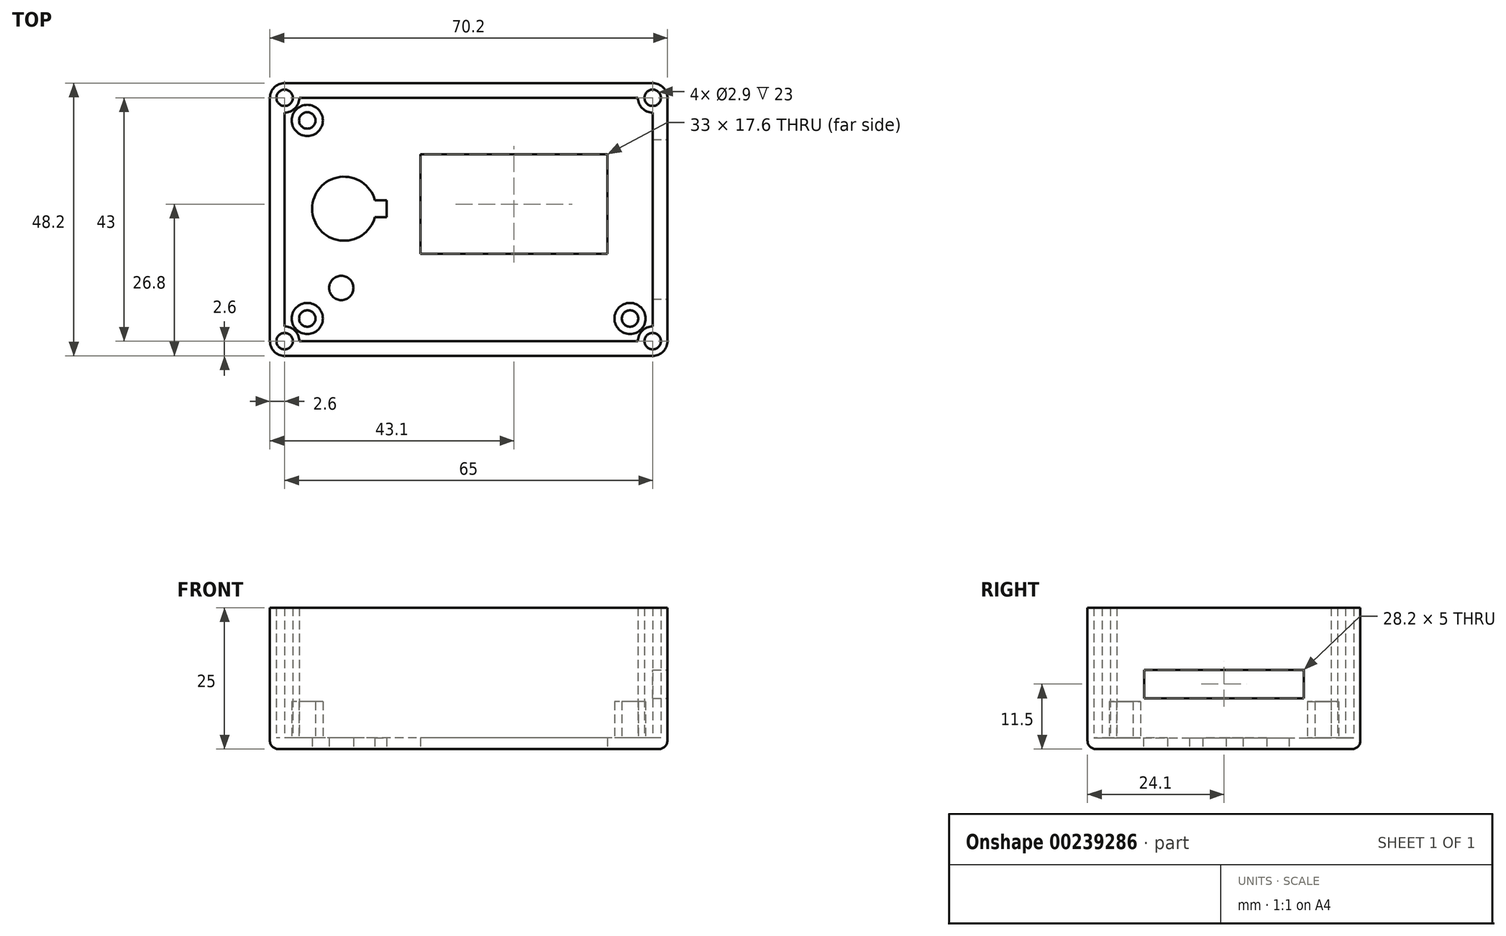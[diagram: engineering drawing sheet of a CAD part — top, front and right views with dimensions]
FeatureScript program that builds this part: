
annotation { "Feature Type Name" : "Feature", "Feature Type Description" : "" }
export const myFeature = defineFeature(function(context is Context, id is Id, definition is map)
    precondition{}
    {
        {
            var Q0;
            Q0=qCreatedBy(makeId("Top.planeOp"),FACE);
            var sketch = newSketch(context, id + "F0", { "sketchPlane" : qUnion([Q0])});
            skLineSegment(sketch, "E0.bottom", {"start": v(35.1, -24.1) * mm, "end": v(-35.1, -24.1) * mm});
            skLineSegment(sketch, "E0.top", {"start": v(35.1, 24.1) * mm, "end": v(-35.1, 24.1) * mm});
            skLineSegment(sketch, "E0.left", {"start": v(35.1, -24.1) * mm, "end": v(35.1, 24.1) * mm});
            skLineSegment(sketch, "E0.right", {"start": v(-35.1, -24.1) * mm, "end": v(-35.1, 24.1) * mm});
            skPoint(sketch, "E0.middle", {"position": v(0, 0) * mm});
            skLineSegment(sketch, "E1.bottom", {"start": v(28.5, -17.5) * mm, "end": v(-28.5, -17.5) * mm});
            skLineSegment(sketch, "E1.top", {"start": v(28.5, 17.5) * mm, "end": v(-28.5, 17.5) * mm});
            skLineSegment(sketch, "E1.left", {"start": v(28.5, -17.5) * mm, "end": v(28.5, 17.5) * mm});
            skLineSegment(sketch, "E1.right", {"start": v(-28.5, -17.5) * mm, "end": v(-28.5, 17.5) * mm});
            skLineSegment(sketch, "E2.bottom", {"start": v(-32.5, 21.5) * mm, "end": v(32.5, 21.5) * mm});
            skLineSegment(sketch, "E2.top", {"start": v(-32.5, -21.5) * mm, "end": v(32.5, -21.5) * mm});
            skLineSegment(sketch, "E2.left", {"start": v(-32.5, 21.5) * mm, "end": v(-32.5, -21.5) * mm});
            skLineSegment(sketch, "E2.right", {"start": v(32.5, 21.5) * mm, "end": v(32.5, -21.5) * mm});
            skCircle(sketch, "E3", {"center": v(-32.5, 21.5) * mm, "radius": 2.6 * mm});
            skCircle(sketch, "E4", {"center": v(-32.5, -21.5) * mm, "radius": 2.6 * mm});
            skCircle(sketch, "E5", {"center": v(32.5, -21.5) * mm, "radius": 2.6 * mm});
            skCircle(sketch, "E6", {"center": v(32.5, -21.5) * mm, "radius": 1.45 * mm});
            skCircle(sketch, "E7", {"center": v(-32.5, -21.5) * mm, "radius": 1.45 * mm});
            skCircle(sketch, "E8", {"center": v(32.5, 21.5) * mm, "radius": 2.6 * mm});
            skCircle(sketch, "E9", {"center": v(32.5, 21.5) * mm, "radius": 1.45 * mm});
            skCircle(sketch, "E10", {"center": v(-32.5, 21.5) * mm, "radius": 1.45 * mm});
            skCircle(sketch, "E11", {"center": v(-28.5, 17.5) * mm, "radius": 2.75 * mm});
            skCircle(sketch, "E12", {"center": v(-28.5, 17.5) * mm, "radius": 1.45 * mm});
            skCircle(sketch, "E13", {"center": v(28.5, -17.5) * mm, "radius": 1.45 * mm});
            skCircle(sketch, "E14", {"center": v(28.5, -17.5) * mm, "radius": 2.75 * mm});
            skCircle(sketch, "E15", {"center": v(-28.5, -17.5) * mm, "radius": 1.45 * mm});
            skCircle(sketch, "E16", {"center": v(-28.5, -17.5) * mm, "radius": 2.75 * mm});
            skCircle(sketch, "E17", {"center": v(-22, 1.9) * mm, "radius": 5.65 * mm});
            skCircle(sketch, "E18", {"center": v(-22.5, -12.1) * mm, "radius": 2.15 * mm});
            skLineSegment(sketch, "E19.bottom", {"start": v(24.5, -6.1) * mm, "end": v(-8.5, -6.1) * mm});
            skLineSegment(sketch, "E19.top", {"start": v(24.5, 11.5) * mm, "end": v(-8.5, 11.5) * mm});
            skLineSegment(sketch, "E19.left", {"start": v(24.5, -6.1) * mm, "end": v(24.5, 11.5) * mm});
            skLineSegment(sketch, "E19.right", {"start": v(-8.5, -6.1) * mm, "end": v(-8.5, 11.5) * mm});
            skPoint(sketch, "E19.middle", {"position": v(8, 2.7) * mm});
            skLineSegment(sketch, "E20.bottom", {"start": v(-22, 3.4) * mm, "end": v(-14.5, 3.4) * mm});
            skLineSegment(sketch, "E20.top", {"start": v(-22, 0.4) * mm, "end": v(-14.5, 0.4) * mm});
            skLineSegment(sketch, "E20.left", {"start": v(-22, 3.4) * mm, "end": v(-22, 0.4) * mm});
            skLineSegment(sketch, "E20.right", {"start": v(-14.5, 3.4) * mm, "end": v(-14.5, 0.4) * mm});
            skSolve(sketch);
        }
        {
            var Q0;
            {var subQ0=sQuery(id+"F0.wireOp",EDGE,"E1.right");var subQ1=sQuery(id+"F0.wireOp",EDGE,"E1.bottom");var subQ2=makeQuery(id+"F0.imprint","INTERSECT",VERTEX,{"derivedFrom":[subQ1,subQ0]});Q0=makeQuery(id+"F0.imprint","IMPRINT",FACE,{"disambiguationData":[TD([[makeQuery(id+"F0.imprint","IMPRINT",EDGE,{"disambiguationData":[TD([[subQ2,1.0]])],"derivedFrom":subQ1}),1.0]])]});}
            var Q1;
            {var subQ0=sQuery(id+"F0.wireOp",EDGE,"E1.right");var subQ1=sQuery(id+"F0.wireOp",EDGE,"E1.bottom");var subQ2=makeQuery(id+"F0.imprint","INTERSECT",VERTEX,{"derivedFrom":[subQ1,subQ0]});Q1=makeQuery(id+"F0.imprint","IMPRINT",FACE,{"disambiguationData":[TD([[makeQuery(id+"F0.imprint","IMPRINT",EDGE,{"disambiguationData":[TD([[subQ2,1.0]])],"derivedFrom":subQ1}),-1.0]])]});}
            var Q2;
            {var subQ5=sQuery(id+"F0.wireOp",EDGE,"E2.top");var subQ8=sQuery(id+"F0.wireOp",EDGE,"E7");var subQ10=makeQuery(id+"F0.imprint","INTERSECT",VERTEX,{"derivedFrom":[subQ5,subQ8]});Q2=makeQuery(id+"F0.imprint","IMPRINT",FACE,{"disambiguationData":[TD([[makeQuery(id+"F0.imprint","IMPRINT",EDGE,{"disambiguationData":[TD([[subQ10,-1.0]])],"derivedFrom":subQ5}),1.0]])]});}
            var Q3;
            {var subQ0=sQuery(id+"F0.wireOp",EDGE,"E2.left");var subQ1=sQuery(id+"F0.wireOp",EDGE,"E2.top");var subQ2=makeQuery(id+"F0.imprint","INTERSECT",VERTEX,{"derivedFrom":[subQ1,subQ0]});Q3=makeQuery(id+"F0.imprint","IMPRINT",FACE,{"disambiguationData":[TD([[makeQuery(id+"F0.imprint","IMPRINT",EDGE,{"disambiguationData":[TD([[subQ2,-1.0]])],"derivedFrom":subQ1}),1.0]])]});}
            var Q4;
            {var subQ0=sQuery(id+"F0.wireOp",EDGE,"E2.left");var subQ1=sQuery(id+"F0.wireOp",EDGE,"E2.top");var subQ2=makeQuery(id+"F0.imprint","INTERSECT",VERTEX,{"derivedFrom":[subQ1,subQ0]});Q4=makeQuery(id+"F0.imprint","IMPRINT",FACE,{"disambiguationData":[TD([[makeQuery(id+"F0.imprint","IMPRINT",EDGE,{"disambiguationData":[TD([[subQ2,-1.0]])],"derivedFrom":subQ1}),-1.0]])]});}
            var Q5;
            {var subQ3=sQuery(id+"F0.wireOp",EDGE,"E7");var subQ4=sQuery(id+"F0.wireOp",EDGE,"E2.top");var subQ5=makeQuery(id+"F0.imprint","INTERSECT",VERTEX,{"derivedFrom":[subQ4,subQ3]});Q5=makeQuery(id+"F0.imprint","IMPRINT",FACE,{"disambiguationData":[TD([[makeQuery(id+"F0.imprint","IMPRINT",EDGE,{"disambiguationData":[TD([[subQ5,-1.0]])],"derivedFrom":subQ4}),-1.0]])]});}
            var Q6;
            {var subQ0=sQuery(id+"F0.wireOp",EDGE,"E5");var subQ1=sQuery(id+"F0.wireOp",EDGE,"E0.bottom");var subQ2=makeQuery(id+"F0.imprint","INTERSECT",VERTEX,{"derivedFrom":[subQ1,subQ0]});Q6=makeQuery(id+"F0.imprint","IMPRINT",FACE,{"disambiguationData":[TD([[makeQuery(id+"F0.imprint","IMPRINT",EDGE,{"disambiguationData":[TD([[subQ2,-1.0]])],"derivedFrom":subQ1}),-1.0]])]});}
            var Q7;
            {var subQ0=sQuery(id+"F0.wireOp",EDGE,"E4");var subQ1=sQuery(id+"F0.wireOp",EDGE,"E0.right");var subQ2=makeQuery(id+"F0.imprint","INTERSECT",VERTEX,{"derivedFrom":[subQ1,subQ0]});Q7=makeQuery(id+"F0.imprint","IMPRINT",FACE,{"disambiguationData":[TD([[makeQuery(id+"F0.imprint","IMPRINT",EDGE,{"disambiguationData":[TD([[subQ2,-1.0]])],"derivedFrom":subQ1}),-1.0]])]});}
            var Q8;
            {var subQ0=sQuery(id+"F0.wireOp",EDGE,"E8");var subQ5=sQuery(id+"F0.wireOp",EDGE,"E2.bottom");var subQ6=makeQuery(id+"F0.imprint","INTERSECT",VERTEX,{"derivedFrom":[subQ5,subQ0]});Q8=makeQuery(id+"F0.imprint","IMPRINT",FACE,{"disambiguationData":[TD([[makeQuery(id+"F0.imprint","IMPRINT",EDGE,{"disambiguationData":[TD([[subQ6,-1.0]])],"derivedFrom":subQ5}),-1.0]])]});}
            var Q9;
            {var subQ0=sQuery(id+"F0.wireOp",EDGE,"E2.right");var subQ1=sQuery(id+"F0.wireOp",EDGE,"E2.bottom");var subQ2=makeQuery(id+"F0.imprint","INTERSECT",VERTEX,{"derivedFrom":[subQ1,subQ0]});Q9=makeQuery(id+"F0.imprint","IMPRINT",FACE,{"disambiguationData":[TD([[makeQuery(id+"F0.imprint","IMPRINT",EDGE,{"disambiguationData":[TD([[subQ2,1.0]])],"derivedFrom":subQ1}),-1.0]])]});}
            var Q10;
            {var subQ0=sQuery(id+"F0.wireOp",EDGE,"E2.right");var subQ1=sQuery(id+"F0.wireOp",EDGE,"E2.bottom");var subQ2=makeQuery(id+"F0.imprint","INTERSECT",VERTEX,{"derivedFrom":[subQ1,subQ0]});Q10=makeQuery(id+"F0.imprint","IMPRINT",FACE,{"disambiguationData":[TD([[makeQuery(id+"F0.imprint","IMPRINT",EDGE,{"disambiguationData":[TD([[subQ2,1.0]])],"derivedFrom":subQ1}),1.0]])]});}
            var Q11;
            {var subQ0=sQuery(id+"F0.wireOp",EDGE,"E8");var subQ2=sQuery(id+"F0.wireOp",EDGE,"E2.bottom");var subQ3=makeQuery(id+"F0.imprint","INTERSECT",VERTEX,{"derivedFrom":[subQ2,subQ0]});Q11=makeQuery(id+"F0.imprint","IMPRINT",FACE,{"disambiguationData":[TD([[makeQuery(id+"F0.imprint","IMPRINT",EDGE,{"disambiguationData":[TD([[subQ3,-1.0]])],"derivedFrom":subQ2}),1.0]])]});}
            var Q12;
            {var subQ0=sQuery(id+"F0.wireOp",EDGE,"E5");var subQ1=sQuery(id+"F0.wireOp",EDGE,"E0.left");var subQ2=makeQuery(id+"F0.imprint","INTERSECT",VERTEX,{"derivedFrom":[subQ1,subQ0]});Q12=makeQuery(id+"F0.imprint","IMPRINT",FACE,{"disambiguationData":[TD([[makeQuery(id+"F0.imprint","IMPRINT",EDGE,{"disambiguationData":[TD([[subQ2,-1.0]])],"derivedFrom":subQ1}),1.0]])]});}
            var Q13;
            {var subQ0=sQuery(id+"F0.wireOp",EDGE,"E8");var subQ1=sQuery(id+"F0.wireOp",EDGE,"E0.top");var subQ2=makeQuery(id+"F0.imprint","INTERSECT",VERTEX,{"derivedFrom":[subQ1,subQ0]});Q13=makeQuery(id+"F0.imprint","IMPRINT",FACE,{"disambiguationData":[TD([[makeQuery(id+"F0.imprint","IMPRINT",EDGE,{"disambiguationData":[TD([[subQ2,-1.0]])],"derivedFrom":subQ1}),1.0]])]});}
            var Q14;
            {var subQ2=sQuery(id+"F0.wireOp",EDGE,"E2.bottom");var subQ5=sQuery(id+"F0.wireOp",EDGE,"E10");var subQ9=makeQuery(id+"F0.imprint","INTERSECT",VERTEX,{"derivedFrom":[subQ2,subQ5]});Q14=makeQuery(id+"F0.imprint","IMPRINT",FACE,{"disambiguationData":[TD([[makeQuery(id+"F0.imprint","IMPRINT",EDGE,{"disambiguationData":[TD([[subQ9,-1.0]])],"derivedFrom":subQ2}),1.0]])]});}
            var Q15;
            {var subQ0=sQuery(id+"F0.wireOp",EDGE,"E2.left");var subQ1=sQuery(id+"F0.wireOp",EDGE,"E2.bottom");var subQ2=makeQuery(id+"F0.imprint","INTERSECT",VERTEX,{"derivedFrom":[subQ1,subQ0]});Q15=makeQuery(id+"F0.imprint","IMPRINT",FACE,{"disambiguationData":[TD([[makeQuery(id+"F0.imprint","IMPRINT",EDGE,{"disambiguationData":[TD([[subQ2,-1.0]])],"derivedFrom":subQ1}),1.0]])]});}
            var Q16;
            {var subQ0=sQuery(id+"F0.wireOp",EDGE,"E2.left");var subQ1=sQuery(id+"F0.wireOp",EDGE,"E2.bottom");var subQ2=makeQuery(id+"F0.imprint","INTERSECT",VERTEX,{"derivedFrom":[subQ1,subQ0]});Q16=makeQuery(id+"F0.imprint","IMPRINT",FACE,{"disambiguationData":[TD([[makeQuery(id+"F0.imprint","IMPRINT",EDGE,{"disambiguationData":[TD([[subQ2,-1.0]])],"derivedFrom":subQ1}),-1.0]])]});}
            var Q17;
            {var subQ1=sQuery(id+"F0.wireOp",EDGE,"E2.bottom");var subQ5=sQuery(id+"F0.wireOp",EDGE,"E10");var subQ10=makeQuery(id+"F0.imprint","INTERSECT",VERTEX,{"derivedFrom":[subQ1,subQ5]});Q17=makeQuery(id+"F0.imprint","IMPRINT",FACE,{"disambiguationData":[TD([[makeQuery(id+"F0.imprint","IMPRINT",EDGE,{"disambiguationData":[TD([[subQ10,-1.0]])],"derivedFrom":subQ1}),-1.0]])]});}
            var Q18;
            {var subQ0=sQuery(id+"F0.wireOp",EDGE,"E5");var subQ2=sQuery(id+"F0.wireOp",EDGE,"E2.top");var subQ3=makeQuery(id+"F0.imprint","INTERSECT",VERTEX,{"derivedFrom":[subQ2,subQ0]});Q18=makeQuery(id+"F0.imprint","IMPRINT",FACE,{"disambiguationData":[TD([[makeQuery(id+"F0.imprint","IMPRINT",EDGE,{"disambiguationData":[TD([[subQ3,-1.0]])],"derivedFrom":subQ2}),-1.0]])]});}
            var Q19;
            {var subQ0=sQuery(id+"F0.wireOp",EDGE,"E2.right");var subQ1=sQuery(id+"F0.wireOp",EDGE,"E2.top");var subQ2=makeQuery(id+"F0.imprint","INTERSECT",VERTEX,{"derivedFrom":[subQ1,subQ0]});Q19=makeQuery(id+"F0.imprint","IMPRINT",FACE,{"disambiguationData":[TD([[makeQuery(id+"F0.imprint","IMPRINT",EDGE,{"disambiguationData":[TD([[subQ2,1.0]])],"derivedFrom":subQ1}),-1.0]])]});}
            var Q20;
            {var subQ0=sQuery(id+"F0.wireOp",EDGE,"E2.right");var subQ1=sQuery(id+"F0.wireOp",EDGE,"E2.top");var subQ2=makeQuery(id+"F0.imprint","INTERSECT",VERTEX,{"derivedFrom":[subQ1,subQ0]});Q20=makeQuery(id+"F0.imprint","IMPRINT",FACE,{"disambiguationData":[TD([[makeQuery(id+"F0.imprint","IMPRINT",EDGE,{"disambiguationData":[TD([[subQ2,1.0]])],"derivedFrom":subQ1}),1.0]])]});}
            var Q21;
            {var subQ0=sQuery(id+"F0.wireOp",EDGE,"E5");var subQ1=sQuery(id+"F0.wireOp",EDGE,"E2.top");var subQ2=makeQuery(id+"F0.imprint","INTERSECT",VERTEX,{"derivedFrom":[subQ1,subQ0]});Q21=makeQuery(id+"F0.imprint","IMPRINT",FACE,{"disambiguationData":[TD([[makeQuery(id+"F0.imprint","IMPRINT",EDGE,{"disambiguationData":[TD([[subQ2,-1.0]])],"derivedFrom":subQ1}),1.0]])]});}
            var Q22;
            {var subQ0=sQuery(id+"F0.wireOp",EDGE,"E11");var subQ1=sQuery(id+"F0.wireOp",EDGE,"E3");var subQ2=makeQuery(id+"F0.imprint","INTERSECT",VERTEX,{"disambiguationData":[OD(0.0)],"derivedFrom":[subQ1,subQ0]});Q22=makeQuery(id+"F0.imprint","IMPRINT",FACE,{"disambiguationData":[TD([[makeQuery(id+"F0.imprint","IMPRINT",EDGE,{"disambiguationData":[TD([[subQ2,-1.0]])],"derivedFrom":subQ1}),1.0]])]});}
            var Q23;
            {var subQ0=sQuery(id+"F0.wireOp",EDGE,"IzADpKWM-4ooe-A6NS-5X2x-zy27TJBy4O8p");var subQ1=sQuery(id+"F0.wireOp",EDGE,"E8");var subQ2=makeQuery(id+"F0.imprint","INTERSECT",VERTEX,{"disambiguationData":[OD(0.0)],"derivedFrom":[subQ1,subQ0]});Q23=makeQuery(id+"F0.imprint","IMPRINT",FACE,{"disambiguationData":[TD([[makeQuery(id+"F0.imprint","IMPRINT",EDGE,{"disambiguationData":[TD([[subQ2,-1.0]])],"derivedFrom":subQ1}),1.0]])]});}
            var Q24;
            {var subQ0=sQuery(id+"F0.wireOp",EDGE,"E14");var subQ1=sQuery(id+"F0.wireOp",EDGE,"E5");var subQ2=makeQuery(id+"F0.imprint","INTERSECT",VERTEX,{"disambiguationData":[OD(0.0)],"derivedFrom":[subQ1,subQ0]});Q24=makeQuery(id+"F0.imprint","IMPRINT",FACE,{"disambiguationData":[TD([[makeQuery(id+"F0.imprint","IMPRINT",EDGE,{"disambiguationData":[TD([[subQ2,-1.0]])],"derivedFrom":subQ1}),1.0]])]});}
            var Q25;
            {var subQ0=sQuery(id+"F0.wireOp",EDGE,"E16");var subQ1=sQuery(id+"F0.wireOp",EDGE,"E4");var subQ2=makeQuery(id+"F0.imprint","INTERSECT",VERTEX,{"disambiguationData":[OD(0.0)],"derivedFrom":[subQ1,subQ0]});Q25=makeQuery(id+"F0.imprint","IMPRINT",FACE,{"disambiguationData":[TD([[makeQuery(id+"F0.imprint","IMPRINT",EDGE,{"disambiguationData":[TD([[subQ2,-1.0]])],"derivedFrom":subQ1}),1.0]])]});}
            var Q26;
            {var subQ1=sQuery(id+"F0.wireOp",EDGE,"E1.bottom");var subQ5=sQuery(id+"F0.wireOp",EDGE,"E16");var subQ6=makeQuery(id+"F0.imprint","INTERSECT",VERTEX,{"derivedFrom":[subQ1,subQ5]});Q26=makeQuery(id+"F0.imprint","IMPRINT",FACE,{"disambiguationData":[TD([[makeQuery(id+"F0.imprint","IMPRINT",EDGE,{"disambiguationData":[TD([[subQ6,-1.0]])],"derivedFrom":subQ1}),1.0]])]});}
            var Q27;
            {var subQ5=sQuery(id+"F0.wireOp",EDGE,"E1.right");var subQ9=sQuery(id+"F0.wireOp",EDGE,"E16");var subQ11=makeQuery(id+"F0.imprint","INTERSECT",VERTEX,{"derivedFrom":[subQ5,subQ9]});Q27=makeQuery(id+"F0.imprint","IMPRINT",FACE,{"disambiguationData":[TD([[makeQuery(id+"F0.imprint","IMPRINT",EDGE,{"disambiguationData":[TD([[subQ11,-1.0]])],"derivedFrom":subQ5}),1.0]])]});}
            var Q28;
            {var subQ0=sQuery(id+"F0.wireOp",EDGE,"E16");var subQ1=sQuery(id+"F0.wireOp",EDGE,"E1.bottom");var subQ2=makeQuery(id+"F0.imprint","INTERSECT",VERTEX,{"derivedFrom":[subQ1,subQ0]});Q28=makeQuery(id+"F0.imprint","IMPRINT",FACE,{"disambiguationData":[TD([[makeQuery(id+"F0.imprint","IMPRINT",EDGE,{"disambiguationData":[TD([[subQ2,-1.0]])],"derivedFrom":subQ1}),-1.0]])]});}
            var Q29;
            {var subQ3=sQuery(id+"F0.wireOp",EDGE,"E14");var subQ5=sQuery(id+"F0.wireOp",EDGE,"E1.bottom");var subQ6=makeQuery(id+"F0.imprint","INTERSECT",VERTEX,{"derivedFrom":[subQ5,subQ3]});Q29=makeQuery(id+"F0.imprint","IMPRINT",FACE,{"disambiguationData":[TD([[makeQuery(id+"F0.imprint","IMPRINT",EDGE,{"disambiguationData":[TD([[subQ6,-1.0]])],"derivedFrom":subQ5}),1.0]])]});}
            var Q30;
            {var subQ0=sQuery(id+"F0.wireOp",EDGE,"E14");var subQ13=sQuery(id+"F0.wireOp",EDGE,"E1.bottom");var subQ14=makeQuery(id+"F0.imprint","INTERSECT",VERTEX,{"derivedFrom":[subQ13,subQ0]});Q30=makeQuery(id+"F0.imprint","IMPRINT",FACE,{"disambiguationData":[TD([[makeQuery(id+"F0.imprint","IMPRINT",EDGE,{"disambiguationData":[TD([[subQ14,-1.0]])],"derivedFrom":subQ13}),-1.0]])]});}
            var Q31;
            {var subQ0=sQuery(id+"F0.wireOp",EDGE,"E11");var subQ1=sQuery(id+"F0.wireOp",EDGE,"E1.top");var subQ2=makeQuery(id+"F0.imprint","INTERSECT",VERTEX,{"derivedFrom":[subQ1,subQ0]});Q31=makeQuery(id+"F0.imprint","IMPRINT",FACE,{"disambiguationData":[TD([[makeQuery(id+"F0.imprint","IMPRINT",EDGE,{"disambiguationData":[TD([[subQ2,-1.0]])],"derivedFrom":subQ1}),-1.0]])]});}
            var Q32;
            {var subQ0=sQuery(id+"F0.wireOp",EDGE,"E1.right");var subQ1=sQuery(id+"F0.wireOp",EDGE,"E1.top");var subQ2=makeQuery(id+"F0.imprint","INTERSECT",VERTEX,{"derivedFrom":[subQ1,subQ0]});Q32=makeQuery(id+"F0.imprint","IMPRINT",FACE,{"disambiguationData":[TD([[makeQuery(id+"F0.imprint","IMPRINT",EDGE,{"disambiguationData":[TD([[subQ2,1.0]])],"derivedFrom":subQ1}),-1.0]])]});}
            var Q33;
            {var subQ0=sQuery(id+"F0.wireOp",EDGE,"E11");var subQ1=sQuery(id+"F0.wireOp",EDGE,"E1.top");var subQ2=makeQuery(id+"F0.imprint","INTERSECT",VERTEX,{"derivedFrom":[subQ1,subQ0]});Q33=makeQuery(id+"F0.imprint","IMPRINT",FACE,{"disambiguationData":[TD([[makeQuery(id+"F0.imprint","IMPRINT",EDGE,{"disambiguationData":[TD([[subQ2,-1.0]])],"derivedFrom":subQ1}),1.0]])]});}
            var Q34;
            {var subQ0=sQuery(id+"F0.wireOp",EDGE,"E1.right");var subQ1=sQuery(id+"F0.wireOp",EDGE,"E1.top");var subQ2=makeQuery(id+"F0.imprint","INTERSECT",VERTEX,{"derivedFrom":[subQ1,subQ0]});Q34=makeQuery(id+"F0.imprint","IMPRINT",FACE,{"disambiguationData":[TD([[makeQuery(id+"F0.imprint","IMPRINT",EDGE,{"disambiguationData":[TD([[subQ2,1.0]])],"derivedFrom":subQ1}),1.0]])]});}
            var Q35;
            {var subQ3=sQuery(id+"F0.wireOp",EDGE,"IzADpKWM-4ooe-A6NS-5X2x-zy27TJBy4O8p");var subQ9=sQuery(id+"F0.wireOp",EDGE,"E1.top");var subQ10=makeQuery(id+"F0.imprint","INTERSECT",VERTEX,{"derivedFrom":[subQ9,subQ3]});Q35=makeQuery(id+"F0.imprint","IMPRINT",FACE,{"disambiguationData":[TD([[makeQuery(id+"F0.imprint","IMPRINT",EDGE,{"disambiguationData":[TD([[subQ10,-1.0]])],"derivedFrom":subQ9}),-1.0]])]});}
            var Q36;
            {var subQ7=sQuery(id+"F0.wireOp",EDGE,"E14");var subQ9=sQuery(id+"F0.wireOp",EDGE,"E1.left");var subQ10=makeQuery(id+"F0.imprint","INTERSECT",VERTEX,{"derivedFrom":[subQ9,subQ7]});Q36=makeQuery(id+"F0.imprint","IMPRINT",FACE,{"disambiguationData":[TD([[makeQuery(id+"F0.imprint","IMPRINT",EDGE,{"disambiguationData":[TD([[subQ10,-1.0]])],"derivedFrom":subQ9}),-1.0]])]});}
            var Q37;
            {var subQ0=sQuery(id+"F0.wireOp",EDGE,"515FwUg4-sH0R-FHhA-I9ZB-DK52WFkX80Ll");var subQ1=sQuery(id+"F0.wireOp",EDGE,"E1.top");var subQ2=makeQuery(id+"F0.imprint","INTERSECT",VERTEX,{"derivedFrom":[subQ1,subQ0]});Q37=makeQuery(id+"F0.imprint","IMPRINT",FACE,{"disambiguationData":[TD([[makeQuery(id+"F0.imprint","IMPRINT",EDGE,{"disambiguationData":[TD([[subQ2,-1.0]])],"derivedFrom":subQ1}),1.0]])]});}
            var Q38;
            {var subQ0=sQuery(id+"F0.wireOp",EDGE,"E1.left");var subQ1=sQuery(id+"F0.wireOp",EDGE,"E1.top");var subQ2=makeQuery(id+"F0.imprint","INTERSECT",VERTEX,{"derivedFrom":[subQ1,subQ0]});Q38=makeQuery(id+"F0.imprint","IMPRINT",FACE,{"disambiguationData":[TD([[makeQuery(id+"F0.imprint","IMPRINT",EDGE,{"disambiguationData":[TD([[subQ2,-1.0]])],"derivedFrom":subQ1}),1.0]])]});}
            var Q39;
            {var subQ0=sQuery(id+"F0.wireOp",EDGE,"E1.left");var subQ1=sQuery(id+"F0.wireOp",EDGE,"E1.top");var subQ2=makeQuery(id+"F0.imprint","INTERSECT",VERTEX,{"derivedFrom":[subQ1,subQ0]});Q39=makeQuery(id+"F0.imprint","IMPRINT",FACE,{"disambiguationData":[TD([[makeQuery(id+"F0.imprint","IMPRINT",EDGE,{"disambiguationData":[TD([[subQ2,-1.0]])],"derivedFrom":subQ1}),-1.0]])]});}
            var Q40;
            {var subQ0=sQuery(id+"F0.wireOp",EDGE,"515FwUg4-sH0R-FHhA-I9ZB-DK52WFkX80Ll");var subQ1=sQuery(id+"F0.wireOp",EDGE,"E1.top");var subQ2=makeQuery(id+"F0.imprint","INTERSECT",VERTEX,{"derivedFrom":[subQ1,subQ0]});Q40=makeQuery(id+"F0.imprint","IMPRINT",FACE,{"disambiguationData":[TD([[makeQuery(id+"F0.imprint","IMPRINT",EDGE,{"disambiguationData":[TD([[subQ2,-1.0]])],"derivedFrom":subQ1}),-1.0]])]});}
            var Q41;
            {var subQ0=sQuery(id+"F0.wireOp",EDGE,"E13");var subQ1=sQuery(id+"F0.wireOp",EDGE,"E1.bottom");var subQ2=makeQuery(id+"F0.imprint","INTERSECT",VERTEX,{"derivedFrom":[subQ1,subQ0]});Q41=makeQuery(id+"F0.imprint","IMPRINT",FACE,{"disambiguationData":[TD([[makeQuery(id+"F0.imprint","IMPRINT",EDGE,{"disambiguationData":[TD([[subQ2,-1.0]])],"derivedFrom":subQ1}),-1.0]])]});}
            var Q42;
            {var subQ0=sQuery(id+"F0.wireOp",EDGE,"E1.left");var subQ1=sQuery(id+"F0.wireOp",EDGE,"E1.bottom");var subQ2=makeQuery(id+"F0.imprint","INTERSECT",VERTEX,{"derivedFrom":[subQ1,subQ0]});Q42=makeQuery(id+"F0.imprint","IMPRINT",FACE,{"disambiguationData":[TD([[makeQuery(id+"F0.imprint","IMPRINT",EDGE,{"disambiguationData":[TD([[subQ2,-1.0]])],"derivedFrom":subQ1}),-1.0]])]});}
            var Q43;
            {var subQ0=sQuery(id+"F0.wireOp",EDGE,"E1.left");var subQ1=sQuery(id+"F0.wireOp",EDGE,"E1.bottom");var subQ2=makeQuery(id+"F0.imprint","INTERSECT",VERTEX,{"derivedFrom":[subQ1,subQ0]});Q43=makeQuery(id+"F0.imprint","IMPRINT",FACE,{"disambiguationData":[TD([[makeQuery(id+"F0.imprint","IMPRINT",EDGE,{"disambiguationData":[TD([[subQ2,-1.0]])],"derivedFrom":subQ1}),1.0]])]});}
            var Q44;
            {var subQ0=sQuery(id+"F0.wireOp",EDGE,"E13");var subQ1=sQuery(id+"F0.wireOp",EDGE,"E1.bottom");var subQ2=makeQuery(id+"F0.imprint","INTERSECT",VERTEX,{"derivedFrom":[subQ1,subQ0]});Q44=makeQuery(id+"F0.imprint","IMPRINT",FACE,{"disambiguationData":[TD([[makeQuery(id+"F0.imprint","IMPRINT",EDGE,{"disambiguationData":[TD([[subQ2,-1.0]])],"derivedFrom":subQ1}),1.0]])]});}
            var Q45;
            {var subQ0=sQuery(id+"F0.wireOp",EDGE,"a319df9c-fd4a-480b-93c2-d0a2a8c2ecbd.bottom");var subQ1=sQuery(id+"F0.wireOp",EDGE,"IzADpKWM-4ooe-A6NS-5X2x-zy27TJBy4O8p");var subQ2=makeQuery(id+"F0.imprint","INTERSECT",VERTEX,{"derivedFrom":[subQ1,subQ0]});Q45=makeQuery(id+"F0.imprint","IMPRINT",FACE,{"disambiguationData":[TD([[makeQuery(id+"F0.imprint","IMPRINT",EDGE,{"disambiguationData":[TD([[subQ2,-1.0]])],"derivedFrom":subQ1}),1.0]])]});}
            var Q46;
            {var subQ1=sQuery(id+"F0.wireOp",EDGE,"a319df9c-fd4a-480b-93c2-d0a2a8c2ecbd.top");Q46=makeQuery(id+"F0.imprint","IMPRINT",FACE,{"disambiguationData":[TD([[makeQuery(id+"F0.imprint","IMPRINT",EDGE,{"derivedFrom":subQ1}),1.0]])]});}
            extrude(context, id + "F1", {"entities" : qUnion([Q0, Q1, Q2, Q3, Q4, Q5, Q6, Q7, Q8, Q9, Q10, Q11, Q12, Q13, Q14, Q15, Q16, Q17, Q18, Q19, Q20, Q21, Q22, Q23, Q24, Q25, Q26, Q27, Q28, Q29, Q30, Q31, Q32, Q33, Q34, Q35, Q36, Q37, Q38, Q39, Q40, Q41, Q42, Q43, Q44, Q45, Q46]), "depth" : 2 * mm});
        }
        {
            var Q0;
            {var subQ1=sQuery(id+"F0.wireOp",EDGE,"E2.bottom");var subQ5=sQuery(id+"F0.wireOp",EDGE,"E10");var subQ10=makeQuery(id+"F0.imprint","INTERSECT",VERTEX,{"derivedFrom":[subQ1,subQ5]});Q0=makeQuery(id+"F0.imprint","IMPRINT",FACE,{"disambiguationData":[TD([[makeQuery(id+"F0.imprint","IMPRINT",EDGE,{"disambiguationData":[TD([[subQ10,-1.0]])],"derivedFrom":subQ1}),-1.0]])]});}
            var Q1;
            {var subQ2=sQuery(id+"F0.wireOp",EDGE,"E2.bottom");var subQ5=sQuery(id+"F0.wireOp",EDGE,"E10");var subQ9=makeQuery(id+"F0.imprint","INTERSECT",VERTEX,{"derivedFrom":[subQ2,subQ5]});Q1=makeQuery(id+"F0.imprint","IMPRINT",FACE,{"disambiguationData":[TD([[makeQuery(id+"F0.imprint","IMPRINT",EDGE,{"disambiguationData":[TD([[subQ9,-1.0]])],"derivedFrom":subQ2}),1.0]])]});}
            var Q2;
            {var subQ0=sQuery(id+"F0.wireOp",EDGE,"E4");var subQ1=sQuery(id+"F0.wireOp",EDGE,"E0.right");var subQ2=makeQuery(id+"F0.imprint","INTERSECT",VERTEX,{"derivedFrom":[subQ1,subQ0]});Q2=makeQuery(id+"F0.imprint","IMPRINT",FACE,{"disambiguationData":[TD([[makeQuery(id+"F0.imprint","IMPRINT",EDGE,{"disambiguationData":[TD([[subQ2,-1.0]])],"derivedFrom":subQ1}),-1.0]])]});}
            var Q3;
            {var subQ0=sQuery(id+"F0.wireOp",EDGE,"E8");var subQ1=sQuery(id+"F0.wireOp",EDGE,"E0.top");var subQ2=makeQuery(id+"F0.imprint","INTERSECT",VERTEX,{"derivedFrom":[subQ1,subQ0]});Q3=makeQuery(id+"F0.imprint","IMPRINT",FACE,{"disambiguationData":[TD([[makeQuery(id+"F0.imprint","IMPRINT",EDGE,{"disambiguationData":[TD([[subQ2,-1.0]])],"derivedFrom":subQ1}),1.0]])]});}
            var Q4;
            {var subQ0=sQuery(id+"F0.wireOp",EDGE,"E8");var subQ5=sQuery(id+"F0.wireOp",EDGE,"E2.bottom");var subQ6=makeQuery(id+"F0.imprint","INTERSECT",VERTEX,{"derivedFrom":[subQ5,subQ0]});Q4=makeQuery(id+"F0.imprint","IMPRINT",FACE,{"disambiguationData":[TD([[makeQuery(id+"F0.imprint","IMPRINT",EDGE,{"disambiguationData":[TD([[subQ6,-1.0]])],"derivedFrom":subQ5}),-1.0]])]});}
            var Q5;
            {var subQ0=sQuery(id+"F0.wireOp",EDGE,"E8");var subQ2=sQuery(id+"F0.wireOp",EDGE,"E2.bottom");var subQ3=makeQuery(id+"F0.imprint","INTERSECT",VERTEX,{"derivedFrom":[subQ2,subQ0]});Q5=makeQuery(id+"F0.imprint","IMPRINT",FACE,{"disambiguationData":[TD([[makeQuery(id+"F0.imprint","IMPRINT",EDGE,{"disambiguationData":[TD([[subQ3,-1.0]])],"derivedFrom":subQ2}),1.0]])]});}
            var Q6;
            {var subQ0=sQuery(id+"F0.wireOp",EDGE,"E5");var subQ1=sQuery(id+"F0.wireOp",EDGE,"E0.left");var subQ2=makeQuery(id+"F0.imprint","INTERSECT",VERTEX,{"derivedFrom":[subQ1,subQ0]});Q6=makeQuery(id+"F0.imprint","IMPRINT",FACE,{"disambiguationData":[TD([[makeQuery(id+"F0.imprint","IMPRINT",EDGE,{"disambiguationData":[TD([[subQ2,-1.0]])],"derivedFrom":subQ1}),1.0]])]});}
            var Q7;
            {var subQ0=sQuery(id+"F0.wireOp",EDGE,"E5");var subQ2=sQuery(id+"F0.wireOp",EDGE,"E2.top");var subQ3=makeQuery(id+"F0.imprint","INTERSECT",VERTEX,{"derivedFrom":[subQ2,subQ0]});Q7=makeQuery(id+"F0.imprint","IMPRINT",FACE,{"disambiguationData":[TD([[makeQuery(id+"F0.imprint","IMPRINT",EDGE,{"disambiguationData":[TD([[subQ3,-1.0]])],"derivedFrom":subQ2}),-1.0]])]});}
            var Q8;
            {var subQ0=sQuery(id+"F0.wireOp",EDGE,"E5");var subQ1=sQuery(id+"F0.wireOp",EDGE,"E2.top");var subQ2=makeQuery(id+"F0.imprint","INTERSECT",VERTEX,{"derivedFrom":[subQ1,subQ0]});Q8=makeQuery(id+"F0.imprint","IMPRINT",FACE,{"disambiguationData":[TD([[makeQuery(id+"F0.imprint","IMPRINT",EDGE,{"disambiguationData":[TD([[subQ2,-1.0]])],"derivedFrom":subQ1}),1.0]])]});}
            var Q9;
            {var subQ0=sQuery(id+"F0.wireOp",EDGE,"E5");var subQ1=sQuery(id+"F0.wireOp",EDGE,"E0.bottom");var subQ2=makeQuery(id+"F0.imprint","INTERSECT",VERTEX,{"derivedFrom":[subQ1,subQ0]});Q9=makeQuery(id+"F0.imprint","IMPRINT",FACE,{"disambiguationData":[TD([[makeQuery(id+"F0.imprint","IMPRINT",EDGE,{"disambiguationData":[TD([[subQ2,-1.0]])],"derivedFrom":subQ1}),-1.0]])]});}
            var Q10;
            {var subQ5=sQuery(id+"F0.wireOp",EDGE,"E2.top");var subQ8=sQuery(id+"F0.wireOp",EDGE,"E7");var subQ10=makeQuery(id+"F0.imprint","INTERSECT",VERTEX,{"derivedFrom":[subQ5,subQ8]});Q10=makeQuery(id+"F0.imprint","IMPRINT",FACE,{"disambiguationData":[TD([[makeQuery(id+"F0.imprint","IMPRINT",EDGE,{"disambiguationData":[TD([[subQ10,-1.0]])],"derivedFrom":subQ5}),1.0]])]});}
            var Q11;
            {var subQ3=sQuery(id+"F0.wireOp",EDGE,"E7");var subQ4=sQuery(id+"F0.wireOp",EDGE,"E2.top");var subQ5=makeQuery(id+"F0.imprint","INTERSECT",VERTEX,{"derivedFrom":[subQ4,subQ3]});Q11=makeQuery(id+"F0.imprint","IMPRINT",FACE,{"disambiguationData":[TD([[makeQuery(id+"F0.imprint","IMPRINT",EDGE,{"disambiguationData":[TD([[subQ5,-1.0]])],"derivedFrom":subQ4}),-1.0]])]});}
            extrude(context, id + "F2", {"entities" : qUnion([Q0, Q1, Q2, Q3, Q4, Q5, Q6, Q7, Q8, Q9, Q10, Q11]), "operationType" : NewBodyOperationType.ADD, "depth" : 25 * mm});
        }
        {
            var Q0;
            {var subQ0=sQuery(id+"F0.wireOp",EDGE,"E11");var subQ1=sQuery(id+"F0.wireOp",EDGE,"E1.top");var subQ2=makeQuery(id+"F0.imprint","INTERSECT",VERTEX,{"derivedFrom":[subQ1,subQ0]});Q0=makeQuery(id+"F0.imprint","IMPRINT",FACE,{"disambiguationData":[TD([[makeQuery(id+"F0.imprint","IMPRINT",EDGE,{"disambiguationData":[TD([[subQ2,-1.0]])],"derivedFrom":subQ1}),-1.0]])]});}
            var Q1;
            {var subQ0=sQuery(id+"F0.wireOp",EDGE,"E11");var subQ1=sQuery(id+"F0.wireOp",EDGE,"E3");var subQ2=makeQuery(id+"F0.imprint","INTERSECT",VERTEX,{"disambiguationData":[OD(0.0)],"derivedFrom":[subQ1,subQ0]});Q1=makeQuery(id+"F0.imprint","IMPRINT",FACE,{"disambiguationData":[TD([[makeQuery(id+"F0.imprint","IMPRINT",EDGE,{"disambiguationData":[TD([[subQ2,-1.0]])],"derivedFrom":subQ1}),1.0]])]});}
            var Q2;
            {var subQ0=sQuery(id+"F0.wireOp",EDGE,"E11");var subQ1=sQuery(id+"F0.wireOp",EDGE,"E1.top");var subQ2=makeQuery(id+"F0.imprint","INTERSECT",VERTEX,{"derivedFrom":[subQ1,subQ0]});Q2=makeQuery(id+"F0.imprint","IMPRINT",FACE,{"disambiguationData":[TD([[makeQuery(id+"F0.imprint","IMPRINT",EDGE,{"disambiguationData":[TD([[subQ2,-1.0]])],"derivedFrom":subQ1}),1.0]])]});}
            var Q3;
            {var subQ0=sQuery(id+"F0.wireOp",EDGE,"E13");var subQ1=sQuery(id+"F0.wireOp",EDGE,"E1.bottom");var subQ2=makeQuery(id+"F0.imprint","INTERSECT",VERTEX,{"derivedFrom":[subQ1,subQ0]});Q3=makeQuery(id+"F0.imprint","IMPRINT",FACE,{"disambiguationData":[TD([[makeQuery(id+"F0.imprint","IMPRINT",EDGE,{"disambiguationData":[TD([[subQ2,-1.0]])],"derivedFrom":subQ1}),-1.0]])]});}
            var Q4;
            {var subQ0=sQuery(id+"F0.wireOp",EDGE,"E13");var subQ1=sQuery(id+"F0.wireOp",EDGE,"E1.bottom");var subQ2=makeQuery(id+"F0.imprint","INTERSECT",VERTEX,{"derivedFrom":[subQ1,subQ0]});Q4=makeQuery(id+"F0.imprint","IMPRINT",FACE,{"disambiguationData":[TD([[makeQuery(id+"F0.imprint","IMPRINT",EDGE,{"disambiguationData":[TD([[subQ2,-1.0]])],"derivedFrom":subQ1}),1.0]])]});}
            var Q5;
            {var subQ0=sQuery(id+"F0.wireOp",EDGE,"E16");var subQ1=sQuery(id+"F0.wireOp",EDGE,"E1.bottom");var subQ2=makeQuery(id+"F0.imprint","INTERSECT",VERTEX,{"derivedFrom":[subQ1,subQ0]});Q5=makeQuery(id+"F0.imprint","IMPRINT",FACE,{"disambiguationData":[TD([[makeQuery(id+"F0.imprint","IMPRINT",EDGE,{"disambiguationData":[TD([[subQ2,-1.0]])],"derivedFrom":subQ1}),-1.0]])]});}
            var Q6;
            {var subQ1=sQuery(id+"F0.wireOp",EDGE,"E1.bottom");var subQ5=sQuery(id+"F0.wireOp",EDGE,"E16");var subQ6=makeQuery(id+"F0.imprint","INTERSECT",VERTEX,{"derivedFrom":[subQ1,subQ5]});Q6=makeQuery(id+"F0.imprint","IMPRINT",FACE,{"disambiguationData":[TD([[makeQuery(id+"F0.imprint","IMPRINT",EDGE,{"disambiguationData":[TD([[subQ6,-1.0]])],"derivedFrom":subQ1}),1.0]])]});}
            var Q7;
            {var subQ0=sQuery(id+"F0.wireOp",EDGE,"IzADpKWM-4ooe-A6NS-5X2x-zy27TJBy4O8p");var subQ1=sQuery(id+"F0.wireOp",EDGE,"E8");var subQ2=makeQuery(id+"F0.imprint","INTERSECT",VERTEX,{"disambiguationData":[OD(0.0)],"derivedFrom":[subQ1,subQ0]});Q7=makeQuery(id+"F0.imprint","IMPRINT",FACE,{"disambiguationData":[TD([[makeQuery(id+"F0.imprint","IMPRINT",EDGE,{"disambiguationData":[TD([[subQ2,-1.0]])],"derivedFrom":subQ1}),1.0]])]});}
            var Q8;
            {var subQ0=sQuery(id+"F0.wireOp",EDGE,"E14");var subQ1=sQuery(id+"F0.wireOp",EDGE,"E5");var subQ2=makeQuery(id+"F0.imprint","INTERSECT",VERTEX,{"disambiguationData":[OD(0.0)],"derivedFrom":[subQ1,subQ0]});Q8=makeQuery(id+"F0.imprint","IMPRINT",FACE,{"disambiguationData":[TD([[makeQuery(id+"F0.imprint","IMPRINT",EDGE,{"disambiguationData":[TD([[subQ2,-1.0]])],"derivedFrom":subQ1}),1.0]])]});}
            var Q9;
            {var subQ0=sQuery(id+"F0.wireOp",EDGE,"E16");var subQ1=sQuery(id+"F0.wireOp",EDGE,"E4");var subQ2=makeQuery(id+"F0.imprint","INTERSECT",VERTEX,{"disambiguationData":[OD(0.0)],"derivedFrom":[subQ1,subQ0]});Q9=makeQuery(id+"F0.imprint","IMPRINT",FACE,{"disambiguationData":[TD([[makeQuery(id+"F0.imprint","IMPRINT",EDGE,{"disambiguationData":[TD([[subQ2,-1.0]])],"derivedFrom":subQ1}),1.0]])]});}
            extrude(context, id + "F3", {"entities" : qUnion([Q0, Q1, Q2, Q3, Q4, Q5, Q6, Q7, Q8, Q9]), "operationType" : NewBodyOperationType.ADD, "depth" : 8.4 * mm});
        }
        {
            var Q0;
            Q0=makeQuery(id+"F0.imprint","IMPRINT",FACE,{"disambiguationData":[TD([[makeQuery(id+"F0.imprint","IMPRINT",EDGE,{"derivedFrom":sQuery(id+"F0.wireOp",EDGE,"E19.bottom")}),-1.0]])]});
            var Q1;
            Q1=makeQuery(id+"F0.imprint","IMPRINT",FACE,{"disambiguationData":[TD([[makeQuery(id+"F0.imprint","IMPRINT",EDGE,{"derivedFrom":sQuery(id+"F0.wireOp",EDGE,"E17")}),1.0]])]});
            var Q2;
            Q2=makeQuery(id+"F0.imprint","IMPRINT",FACE,{"disambiguationData":[TD([[makeQuery(id+"F0.imprint","IMPRINT",EDGE,{"derivedFrom":sQuery(id+"F0.wireOp",EDGE,"E18")}),1.0]])]});
            extrude(context, id + "F4", {"entities" : qUnion([Q0, Q1, Q2]), "operationType" : NewBodyOperationType.REMOVE, "oppositeDirection" : true, "depth" : 25 * mm});
        }
        {
            var Q0;
            Q0=makeQuery(id+"F1.opExtrude","CAP_EDGE",EDGE,{"disambiguationData":[OSD([sQuery(id+"F0.wireOp",EDGE,"E0.top")])],"isStart":true});
            fillet(context, id + "F5", {"entities" : qUnion([Q0]), "radius" : 1.5 * mm, "tangentPropagation" : true, "allowEdgeOverflow" : false});
        }
        {
            var Q0;
            {var subQ0=sQuery(id+"F0.wireOp",EDGE,"E0.left");Q0=makeQuery(id+"F2.boolean.opBoolean","MERGE",FACE,{"derivedFrom":[makeQuery(id+"F1.opExtrude","SWEPT_FACE",FACE,{"disambiguationData":[OSD([subQ0])]}),makeQuery(id+"F2.opExtrude","SWEPT_FACE",FACE,{"disambiguationData":[OSD([subQ0])]})]});}
            var sketch = newSketch(context, id + "F6", { "sketchPlane" : qUnion([Q0])});
            skLineSegment(sketch, "E21.bottom", {"start": v(14.1, 9) * mm, "end": v(-14.1, 9) * mm});
            skLineSegment(sketch, "E21.top", {"start": v(14.1, 14) * mm, "end": v(-14.1, 14) * mm});
            skLineSegment(sketch, "E21.left", {"start": v(14.1, 9) * mm, "end": v(14.1, 14) * mm});
            skLineSegment(sketch, "E21.right", {"start": v(-14.1, 9) * mm, "end": v(-14.1, 14) * mm});
            skSolve(sketch);
        }
        {
            var Q0;
            Q0=makeQuery(id+"F6.imprint","IMPRINT",FACE,{"disambiguationData":[TD([[makeQuery(id+"F6.imprint","IMPRINT",EDGE,{"derivedFrom":sQuery(id+"F6.wireOp",EDGE,"E21.bottom")}),-1.0]])]});
            extrude(context, id + "F7", {"entities" : qUnion([Q0]), "operationType" : NewBodyOperationType.REMOVE, "oppositeDirection" : true, "depth" : 3.5 * mm});
        }
    });
